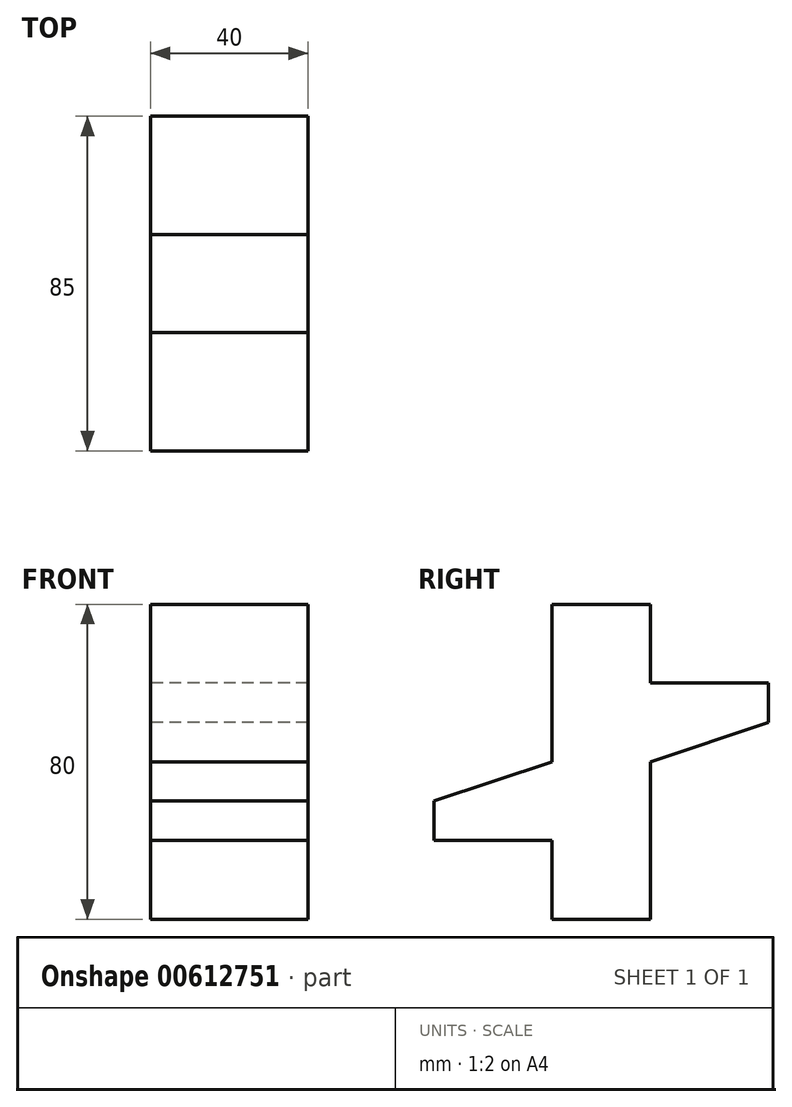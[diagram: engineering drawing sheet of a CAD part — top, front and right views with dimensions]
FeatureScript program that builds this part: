
annotation { "Feature Type Name" : "Feature", "Feature Type Description" : "" }
export const myFeature = defineFeature(function(context is Context, id is Id, definition is map)
    precondition{}
    {
        {
            var Q0;
            Q0=qCreatedBy(makeId("Right.planeOp"),FACE);
            var sketch = newSketch(context, id + "F0", { "sketchPlane" : qUnion([Q0])});
            skLineSegment(sketch, "E0", {"start": v(-23.26, 6.67) * mm, "end": v(1.74, 6.67) * mm});
            skLineSegment(sketch, "E1", {"start": v(1.74, 6.67) * mm, "end": v(1.74, 46.67) * mm});
            skLineSegment(sketch, "E2", {"start": v(-23.26, 6.67) * mm, "end": v(-23.26, 26.67) * mm});
            skLineSegment(sketch, "E3", {"start": v(-23.26, 26.67) * mm, "end": v(-53.26, 26.67) * mm});
            skLineSegment(sketch, "E4", {"start": v(-53.26, 26.67) * mm, "end": v(-53.26, 36.67) * mm});
            skLineSegment(sketch, "E5", {"start": v(-23.26, 6.67) * mm, "end": v(-23.26, 86.67) * mm, "construction": true});
            skLineSegment(sketch, "E6", {"start": v(-23.26, 86.67) * mm, "end": v(-23.26, 46.67) * mm});
            skLineSegment(sketch, "E7", {"start": v(-53.26, 36.67) * mm, "end": v(-23.26, 46.67) * mm});
            skLineSegment(sketch, "E8", {"start": v(-23.26, 86.67) * mm, "end": v(1.74, 86.67) * mm});
            skLineSegment(sketch, "E9", {"start": v(1.74, 86.67) * mm, "end": v(1.74, 66.67) * mm});
            skLineSegment(sketch, "E10", {"start": v(1.74, 66.67) * mm, "end": v(31.74, 66.67) * mm});
            skLineSegment(sketch, "E11", {"start": v(31.74, 66.67) * mm, "end": v(31.74, 56.67) * mm});
            skLineSegment(sketch, "E12", {"start": v(31.74, 56.67) * mm, "end": v(1.74, 46.67) * mm});
            skSolve(sketch);
        }
        {
            var Q0;
            Q0=makeQuery(id+"F0.imprint","IMPRINT",FACE,{"disambiguationData":[TD([[makeQuery(id+"F0.imprint","IMPRINT",EDGE,{"derivedFrom":sQuery(id+"F0.wireOp",EDGE,"E0")}),1.0]])]});
            extrude(context, id + "F1", {"entities" : qUnion([Q0]), "depth" : 40 * mm, "offsetDistance" : 25 * mm});
        }
    });
